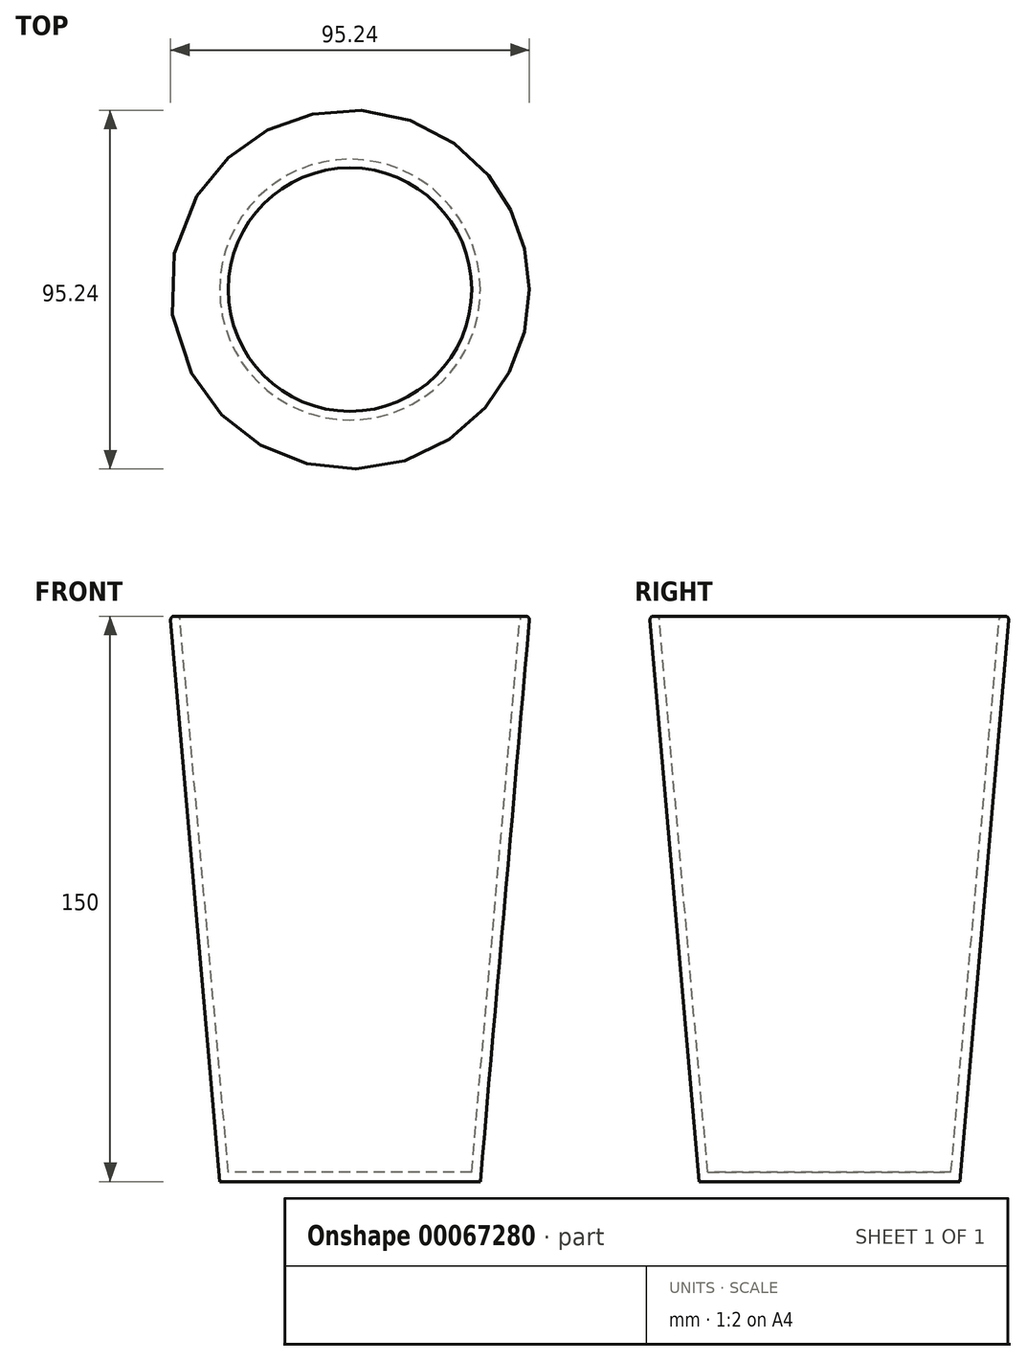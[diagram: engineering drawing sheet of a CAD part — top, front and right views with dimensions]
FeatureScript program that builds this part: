
annotation { "Feature Type Name" : "Feature", "Feature Type Description" : "" }
export const myFeature = defineFeature(function(context is Context, id is Id, definition is map)
    precondition{}
    {
        {
            var Q0;
            Q0=qCreatedBy(makeId("Top.planeOp"),FACE);
            var sketch = newSketch(context, id + "F0", { "sketchPlane" : qUnion([Q0])});
            skCircle(sketch, "E0", {"center": v(0, 0) * mm, "radius": 34.58 * mm});
            skSolve(sketch);
        }
        {
            var Q0;
            Q0=makeQuery(id+"F0.imprint","IMPRINT",FACE,{"disambiguationData":[TD([[makeQuery(id+"F0.imprint","IMPRINT",EDGE,{"derivedFrom":sQuery(id+"F0.wireOp",EDGE,"E0")}),1.0]])]});
            extrude(context, id + "F1", {"entities" : qUnion([Q0]), "depth" : 150 * mm, "hasDraft" : true, "draftAngle" : 5 * degree});
        }
        {
            var Q0;
            Q0=makeQuery(id+"F1.opExtrude","CAP_FACE",FACE,{"disambiguationData":[OSD([sQuery(id+"F0.wireOp",EDGE,"E0")])],"isStart":false});
            shell(context, id + "F2", {"entities" : qUnion([Q0]), "thickness" : 2.5 * mm});
        }
        {
            var Q0;
            Q0=makeQuery(id+"F1.opExtrude","CAP_EDGE",EDGE,{"disambiguationData":[OSD([sQuery(id+"F0.wireOp",EDGE,"E0")])],"isStart":false});
            var Q1;
            {var subQ0=sQuery(id+"F0.wireOp",EDGE,"E0");Q1=makeQuery(id+"F2.opShell","OFFSET_EDGE",EDGE,{"disambiguationData":[OSD([subQ0]),TDD([makeQuery(id+"F1.opExtrude","CAP_EDGE",EDGE,{"disambiguationData":[OSD([subQ0])],"isStart":false})])]});}
            fillet(context, id + "F3", {"entities" : qUnion([Q0, Q1]), "radius" : 1 * mm, "tangentPropagation" : true, "allowEdgeOverflow" : false});
        }
    });
